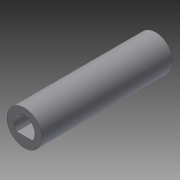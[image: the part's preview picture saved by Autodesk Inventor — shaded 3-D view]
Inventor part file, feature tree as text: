
AUTODESK INVENTOR PART (.ipt)
format: ipt  version: 2013 (Build 170138000, 138)  size: 90,624 bytes
history: native  units: mm
features: extrude x2, sketch x2, plane x1
ambient origin geometry x8: Origin, YZ Plane, XZ Plane, XY Plane, X Axis, Y Axis, Z Axis, Center Point
bodies: Solid1 (feature_tree)
feature tree (5):
  extrude  "Extrusion1"  Depth=4.9mm
  plane  "Work Plane1"
  extrude  "Extrusion6"  Depth=18.5mm TaperAngle=0.0deg
  sketch  "Sketch1"  dims[d0=3.0mm d1=4.9mm]
  sketch  "Sketch6"  dims[d2=0.5mm d4=18.5mm d5=0.0mm d20=4.0mm d21=6.0mm d22=5.0mm d23=0.5mm d24=0.0mm]
